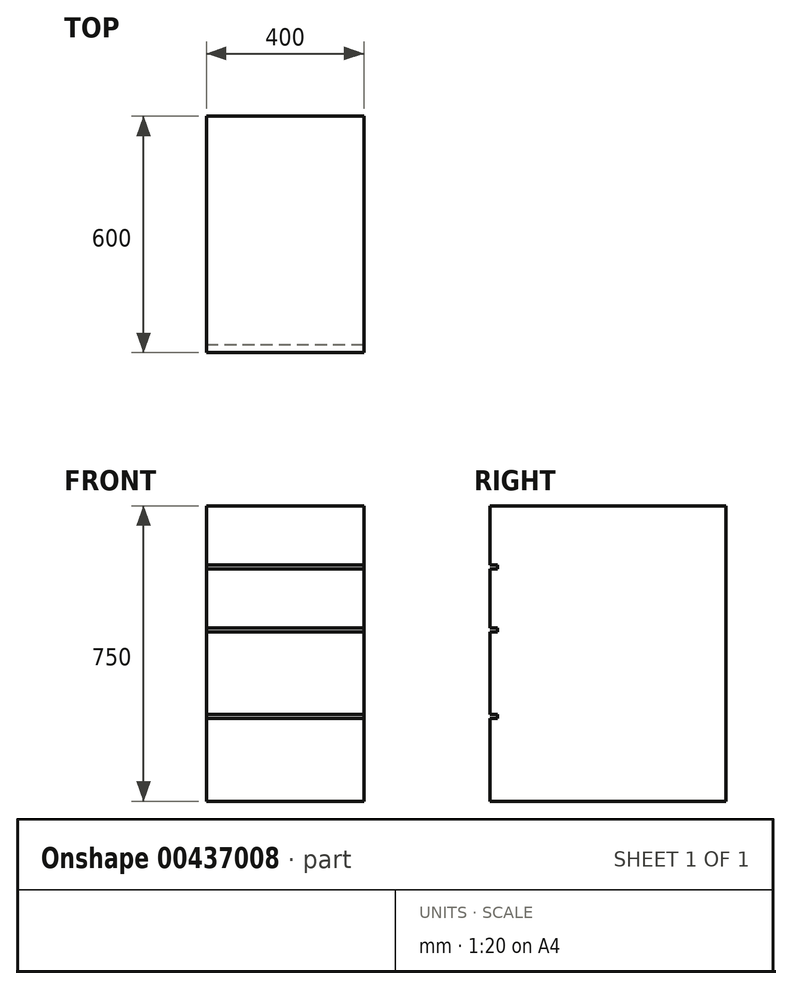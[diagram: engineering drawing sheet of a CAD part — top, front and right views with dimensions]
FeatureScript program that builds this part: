
annotation { "Feature Type Name" : "Feature", "Feature Type Description" : "" }
export const myFeature = defineFeature(function(context is Context, id is Id, definition is map)
    precondition{}
    {
        {
            var Q0;
            Q0=qCreatedBy(makeId("Right.planeOp"),FACE);
            var sketch = newSketch(context, id + "F0", { "sketchPlane" : qUnion([Q0])});
            skLineSegment(sketch, "E0.top", {"start": v(0, 750) * mm, "end": v(-600, 750) * mm});
            skLineSegment(sketch, "E0.left", {"start": v(0, 0) * mm, "end": v(0, 750) * mm});
            skLineSegment(sketch, "E0.right", {"start": v(-600, 0) * mm, "end": v(-600, 750) * mm});
            skLineSegment(sketch, "E1", {"start": v(0, 0) * mm, "end": v(-600, 0) * mm});
            skSolve(sketch);
        }
        {
            var Q0;
            Q0 = qSketchRegion(id + "F0", true);
            extrude(context, id + "F1", {"entities" : qUnion([Q0]), "depth" : 400 * mm});
        }
        {
            var Q0;
            Q0=makeQuery(id+"F1.opExtrude","SWEPT_FACE",FACE,{"disambiguationData":[OSD([sQuery(id+"F0.wireOp",EDGE,"E0.right")])]});
            var sketch = newSketch(context, id + "F2", { "sketchPlane" : qUnion([Q0])});
            skLineSegment(sketch, "E2.bottom", {"start": v(0, 600) * mm, "end": v(400, 600) * mm});
            skLineSegment(sketch, "E2.top", {"start": v(0, 590) * mm, "end": v(400, 590) * mm});
            skLineSegment(sketch, "E2.left", {"start": v(0, 600) * mm, "end": v(0, 590) * mm});
            skLineSegment(sketch, "E2.right", {"start": v(400, 600) * mm, "end": v(400, 590) * mm});
            skLineSegment(sketch, "E3.bottom", {"start": v(0, 440) * mm, "end": v(400, 440) * mm});
            skLineSegment(sketch, "E3.top", {"start": v(0, 430) * mm, "end": v(400, 430) * mm});
            skLineSegment(sketch, "E3.left", {"start": v(0, 440) * mm, "end": v(0, 430) * mm});
            skLineSegment(sketch, "E3.right", {"start": v(400, 440) * mm, "end": v(400, 430) * mm});
            skLineSegment(sketch, "E4.bottom", {"start": v(0, 220) * mm, "end": v(400, 220) * mm});
            skLineSegment(sketch, "E4.top", {"start": v(0, 210) * mm, "end": v(400, 210) * mm});
            skLineSegment(sketch, "E4.left", {"start": v(0, 220) * mm, "end": v(0, 210) * mm});
            skLineSegment(sketch, "E4.right", {"start": v(400, 220) * mm, "end": v(400, 210) * mm});
            skSolve(sketch);
        }
        {
            var Q0;
            Q0 = qSketchRegion(id + "F2", true);
            extrude(context, id + "F3", {"entities" : qUnion([Q0]), "operationType" : NewBodyOperationType.REMOVE, "oppositeDirection" : true, "depth" : 20 * mm});
        }
    });
